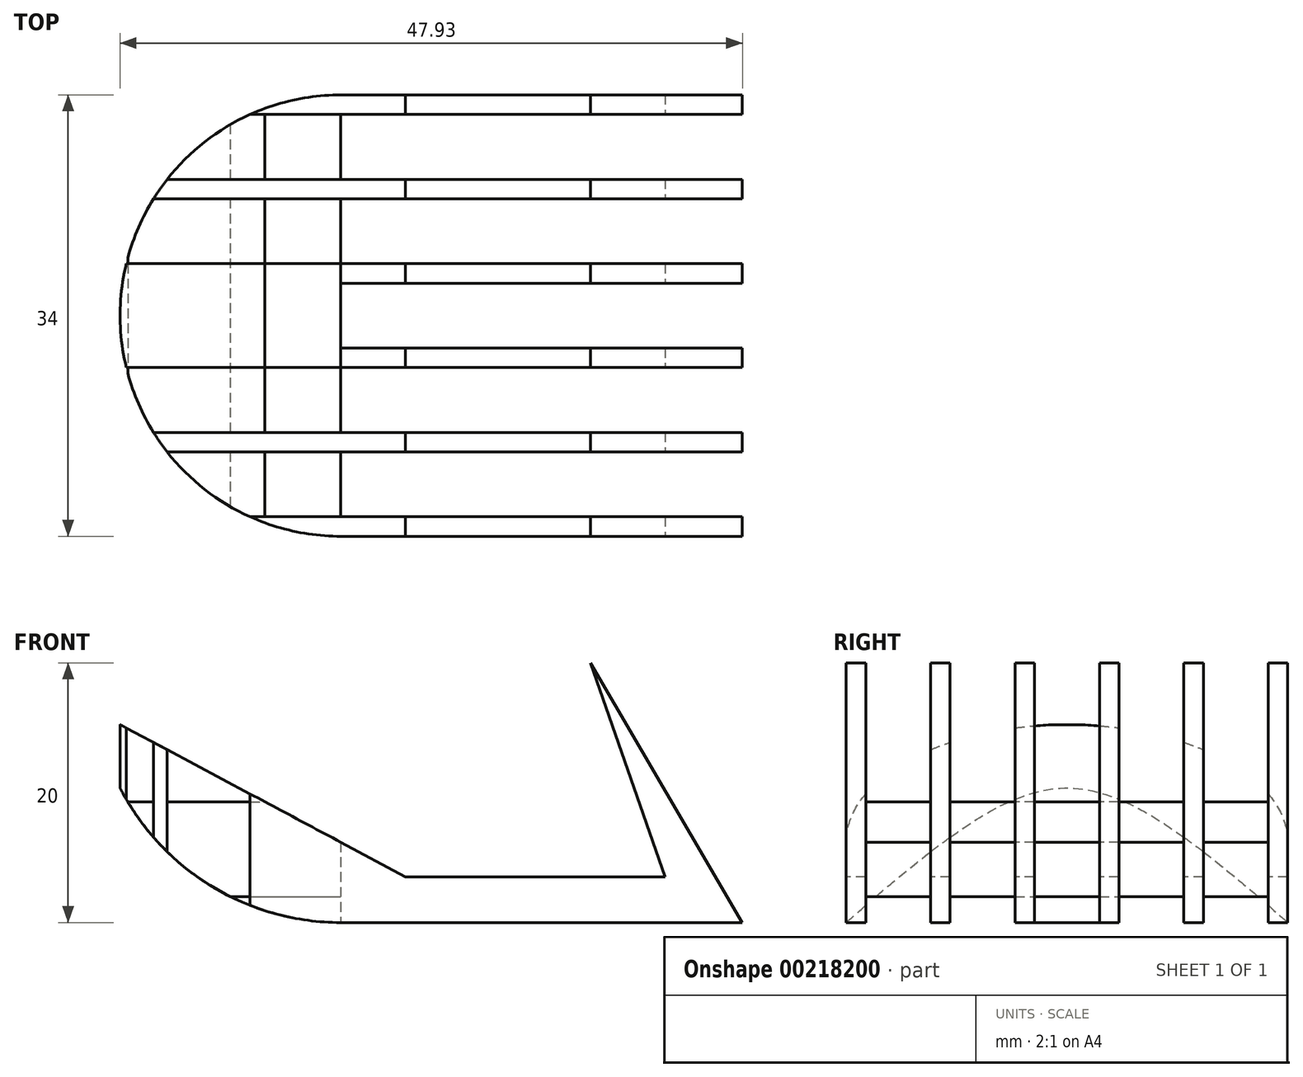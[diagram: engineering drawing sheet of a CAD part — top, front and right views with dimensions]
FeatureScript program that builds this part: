
annotation { "Feature Type Name" : "Feature", "Feature Type Description" : "" }
export const myFeature = defineFeature(function(context is Context, id is Id, definition is map)
    precondition{}
    {
        {
            var Q0;
            Q0=qCreatedBy(makeId("Top.planeOp"),FACE);
            var sketch = newSketch(context, id + "F0", { "sketchPlane" : qUnion([Q0])});
            skLineSegment(sketch, "E0.bottom", {"start": v(0, -14.03) * mm, "end": v(30.93, -14.03) * mm});
            skLineSegment(sketch, "E0.top", {"start": v(0, 19.97) * mm, "end": v(30.93, 19.97) * mm});
            skLineSegment(sketch, "E0.left", {"start": v(0, -14.03) * mm, "end": v(0, 19.97) * mm});
            skLineSegment(sketch, "E0.right", {"start": v(30.93, -14.03) * mm, "end": v(30.93, 19.97) * mm});
            skArc(sketch, "E1", {"start": v(0, 19.97) * mm, "mid": v(-17, 2.97) * mm, "end": v(0, -14.03) * mm});
            skLineSegment(sketch, "E2.bottom", {"start": v(-16.64, -7.53) * mm, "end": v(48.54, -7.53) * mm});
            skLineSegment(sketch, "E2.top", {"start": v(-16.64, -12.53) * mm, "end": v(48.54, -12.53) * mm});
            skLineSegment(sketch, "E2.left", {"start": v(-16.64, -7.53) * mm, "end": v(-16.64, -12.53) * mm});
            skLineSegment(sketch, "E2.right", {"start": v(48.54, -7.53) * mm, "end": v(48.54, -12.53) * mm});
            skPoint(sketch, "E2.middle", {"position": v(15.95, -10.03) * mm});
            skLineSegment(sketch, "E3.0.1.0", {"start": v(-16.64, -6.03) * mm, "end": v(48.54, -6.03) * mm});
            skLineSegment(sketch, "E3.0.1.1", {"start": v(-16.64, -1.03) * mm, "end": v(48.54, -1.03) * mm});
            skLineSegment(sketch, "E3.0.2.0", {"start": v(-16.64, 0.47) * mm, "end": v(48.54, 0.47) * mm});
            skLineSegment(sketch, "E3.0.2.1", {"start": v(-16.64, 5.47) * mm, "end": v(48.54, 5.47) * mm});
            skLineSegment(sketch, "E3.0.3.0", {"start": v(-16.64, 6.97) * mm, "end": v(48.54, 6.97) * mm});
            skLineSegment(sketch, "E3.0.3.1", {"start": v(-16.64, 11.97) * mm, "end": v(48.54, 11.97) * mm});
            skLineSegment(sketch, "E3.0.4.0", {"start": v(-16.64, 13.47) * mm, "end": v(48.54, 13.47) * mm});
            skLineSegment(sketch, "E3.0.4.1", {"start": v(-16.64, 18.47) * mm, "end": v(48.54, 18.47) * mm});
            skLineSegment(sketch, "E3.direction1", {"start": v(-16.64, -12.53) * mm, "end": v(8.36, -12.53) * mm, "construction": true});
            skLineSegment(sketch, "E3.direction2", {"start": v(-16.64, -12.53) * mm, "end": v(-16.64, -6.03) * mm, "construction": true});
            skSolve(sketch);
        }
        {
            var Q0;
            Q0=makeQuery(id+"F0.imprint","IMPRINT",FACE,{"disambiguationData":[TD([[makeQuery(id+"F0.imprint","IMPRINT",EDGE,{"derivedFrom":sQuery(id+"F0.wireOp",EDGE,"E0.bottom")}),1.0]])]});
            var Q1;
            {var subQ0=sQuery(id+"F0.wireOp",EDGE,"E3.0.1.0");var subQ1=sQuery(id+"F0.wireOp",EDGE,"E0.right");var subQ2=makeQuery(id+"F0.imprint","INTERSECT",VERTEX,{"derivedFrom":[subQ1,subQ0]});Q1=makeQuery(id+"F0.imprint","IMPRINT",FACE,{"disambiguationData":[TD([[makeQuery(id+"F0.imprint","IMPRINT",EDGE,{"disambiguationData":[TD([[subQ2,1.0]])],"derivedFrom":subQ1}),1.0]])]});}
            var Q2;
            {var subQ0=sQuery(id+"F0.wireOp",EDGE,"E3.0.1.1");var subQ1=sQuery(id+"F0.wireOp",EDGE,"E0.right");var subQ2=makeQuery(id+"F0.imprint","INTERSECT",VERTEX,{"derivedFrom":[subQ1,subQ0]});Q2=makeQuery(id+"F0.imprint","IMPRINT",FACE,{"disambiguationData":[TD([[makeQuery(id+"F0.imprint","IMPRINT",EDGE,{"disambiguationData":[TD([[subQ2,-1.0]])],"derivedFrom":subQ1}),1.0]])]});}
            var Q3;
            {var subQ0=sQuery(id+"F0.wireOp",EDGE,"E3.0.2.1");var subQ1=sQuery(id+"F0.wireOp",EDGE,"E0.right");var subQ2=makeQuery(id+"F0.imprint","INTERSECT",VERTEX,{"derivedFrom":[subQ1,subQ0]});Q3=makeQuery(id+"F0.imprint","IMPRINT",FACE,{"disambiguationData":[TD([[makeQuery(id+"F0.imprint","IMPRINT",EDGE,{"disambiguationData":[TD([[subQ2,-1.0]])],"derivedFrom":subQ1}),1.0]])]});}
            var Q4;
            {var subQ0=sQuery(id+"F0.wireOp",EDGE,"E3.0.3.1");var subQ1=sQuery(id+"F0.wireOp",EDGE,"E0.right");var subQ2=makeQuery(id+"F0.imprint","INTERSECT",VERTEX,{"derivedFrom":[subQ1,subQ0]});Q4=makeQuery(id+"F0.imprint","IMPRINT",FACE,{"disambiguationData":[TD([[makeQuery(id+"F0.imprint","IMPRINT",EDGE,{"disambiguationData":[TD([[subQ2,-1.0]])],"derivedFrom":subQ1}),1.0]])]});}
            var Q5;
            {var subQ0=sQuery(id+"F0.wireOp",EDGE,"E0.top");Q5=makeQuery(id+"F0.imprint","IMPRINT",FACE,{"disambiguationData":[TD([[makeQuery(id+"F0.imprint","IMPRINT",EDGE,{"derivedFrom":subQ0}),-1.0]])]});}
            var Q6;
            {var subQ0=sQuery(id+"F0.wireOp",EDGE,"E1");var subQ3=sQuery(id+"F0.wireOp",EDGE,"E2.top");var subQ5=makeQuery(id+"F0.imprint","INTERSECT",VERTEX,{"derivedFrom":[subQ0,subQ3]});Q6=makeQuery(id+"F0.imprint","IMPRINT",FACE,{"disambiguationData":[TD([[makeQuery(id+"F0.imprint","IMPRINT",EDGE,{"disambiguationData":[TD([[subQ5,-1.0]])],"derivedFrom":subQ3}),-1.0]])]});}
            var Q7;
            {var subQ0=sQuery(id+"F0.wireOp",EDGE,"E2.bottom");var subQ1=sQuery(id+"F0.wireOp",EDGE,"E0.left");var subQ2=makeQuery(id+"F0.imprint","INTERSECT",VERTEX,{"derivedFrom":[subQ1,subQ0]});Q7=makeQuery(id+"F0.imprint","IMPRINT",FACE,{"disambiguationData":[TD([[makeQuery(id+"F0.imprint","IMPRINT",EDGE,{"disambiguationData":[TD([[subQ2,-1.0]])],"derivedFrom":subQ1}),1.0]])]});}
            var Q8;
            {var subQ0=sQuery(id+"F0.wireOp",EDGE,"E3.0.1.1");var subQ1=sQuery(id+"F0.wireOp",EDGE,"E0.left");var subQ2=makeQuery(id+"F0.imprint","INTERSECT",VERTEX,{"derivedFrom":[subQ1,subQ0]});Q8=makeQuery(id+"F0.imprint","IMPRINT",FACE,{"disambiguationData":[TD([[makeQuery(id+"F0.imprint","IMPRINT",EDGE,{"disambiguationData":[TD([[subQ2,-1.0]])],"derivedFrom":subQ1}),1.0]])]});}
            var Q9;
            {var subQ0=sQuery(id+"F0.wireOp",EDGE,"E3.0.2.1");var subQ1=sQuery(id+"F0.wireOp",EDGE,"E0.left");var subQ2=makeQuery(id+"F0.imprint","INTERSECT",VERTEX,{"derivedFrom":[subQ1,subQ0]});Q9=makeQuery(id+"F0.imprint","IMPRINT",FACE,{"disambiguationData":[TD([[makeQuery(id+"F0.imprint","IMPRINT",EDGE,{"disambiguationData":[TD([[subQ2,-1.0]])],"derivedFrom":subQ1}),1.0]])]});}
            var Q10;
            {var subQ0=sQuery(id+"F0.wireOp",EDGE,"E3.0.3.1");var subQ1=sQuery(id+"F0.wireOp",EDGE,"E0.left");var subQ2=makeQuery(id+"F0.imprint","INTERSECT",VERTEX,{"derivedFrom":[subQ1,subQ0]});Q10=makeQuery(id+"F0.imprint","IMPRINT",FACE,{"disambiguationData":[TD([[makeQuery(id+"F0.imprint","IMPRINT",EDGE,{"disambiguationData":[TD([[subQ2,-1.0]])],"derivedFrom":subQ1}),1.0]])]});}
            var Q11;
            {var subQ0=sQuery(id+"F0.wireOp",EDGE,"E1");var subQ3=sQuery(id+"F0.wireOp",EDGE,"E3.0.4.1");var subQ5=makeQuery(id+"F0.imprint","INTERSECT",VERTEX,{"derivedFrom":[subQ0,subQ3]});Q11=makeQuery(id+"F0.imprint","IMPRINT",FACE,{"disambiguationData":[TD([[makeQuery(id+"F0.imprint","IMPRINT",EDGE,{"disambiguationData":[TD([[subQ5,-1.0]])],"derivedFrom":subQ3}),1.0]])]});}
            extrude(context, id + "F1", {"entities" : qUnion([Q0, Q1, Q2, Q3, Q4, Q5, Q6, Q7, Q8, Q9, Q10, Q11]), "depth" : 20 * mm});
        }
        {
            var Q0;
            {var subQ0=sQuery(id+"F0.wireOp",EDGE,"E2.top");var subQ1=sQuery(id+"F0.wireOp",EDGE,"E0.left");var subQ2=makeQuery(id+"F0.imprint","INTERSECT",VERTEX,{"derivedFrom":[subQ1,subQ0]});Q0=makeQuery(id+"F0.imprint","IMPRINT",FACE,{"disambiguationData":[TD([[makeQuery(id+"F0.imprint","IMPRINT",EDGE,{"disambiguationData":[TD([[subQ2,-1.0]])],"derivedFrom":subQ1}),1.0]])]});}
            var Q1;
            {var subQ0=sQuery(id+"F0.wireOp",EDGE,"E3.0.1.0");var subQ1=sQuery(id+"F0.wireOp",EDGE,"E0.left");var subQ2=makeQuery(id+"F0.imprint","INTERSECT",VERTEX,{"derivedFrom":[subQ1,subQ0]});Q1=makeQuery(id+"F0.imprint","IMPRINT",FACE,{"disambiguationData":[TD([[makeQuery(id+"F0.imprint","IMPRINT",EDGE,{"disambiguationData":[TD([[subQ2,-1.0]])],"derivedFrom":subQ1}),1.0]])]});}
            var Q2;
            {var subQ0=sQuery(id+"F0.wireOp",EDGE,"E3.0.2.0");var subQ1=sQuery(id+"F0.wireOp",EDGE,"E0.left");var subQ2=makeQuery(id+"F0.imprint","INTERSECT",VERTEX,{"derivedFrom":[subQ1,subQ0]});Q2=makeQuery(id+"F0.imprint","IMPRINT",FACE,{"disambiguationData":[TD([[makeQuery(id+"F0.imprint","IMPRINT",EDGE,{"disambiguationData":[TD([[subQ2,-1.0]])],"derivedFrom":subQ1}),1.0]])]});}
            var Q3;
            {var subQ0=sQuery(id+"F0.wireOp",EDGE,"E3.0.3.0");var subQ1=sQuery(id+"F0.wireOp",EDGE,"E0.left");var subQ2=makeQuery(id+"F0.imprint","INTERSECT",VERTEX,{"derivedFrom":[subQ1,subQ0]});Q3=makeQuery(id+"F0.imprint","IMPRINT",FACE,{"disambiguationData":[TD([[makeQuery(id+"F0.imprint","IMPRINT",EDGE,{"disambiguationData":[TD([[subQ2,-1.0]])],"derivedFrom":subQ1}),1.0]])]});}
            var Q4;
            {var subQ0=sQuery(id+"F0.wireOp",EDGE,"E3.0.4.0");var subQ1=sQuery(id+"F0.wireOp",EDGE,"E0.left");var subQ2=makeQuery(id+"F0.imprint","INTERSECT",VERTEX,{"derivedFrom":[subQ1,subQ0]});Q4=makeQuery(id+"F0.imprint","IMPRINT",FACE,{"disambiguationData":[TD([[makeQuery(id+"F0.imprint","IMPRINT",EDGE,{"disambiguationData":[TD([[subQ2,-1.0]])],"derivedFrom":subQ1}),1.0]])]});}
            extrude(context, id + "F2", {"entities" : qUnion([Q0, Q1, Q2, Q3, Q4]), "depth" : 9.3 * mm, "hasSecondDirection" : true, "secondDirectionOppositeDirection" : false, "secondDirectionDepth" : 2 * mm});
        }
        {
            var Q0;
            Q0=makeQuery(id+"F1.opExtrude","SWEPT_FACE",FACE,{"disambiguationData":[OSD([sQuery(id+"F0.wireOp",EDGE,"E0.bottom")])]});
            var sketch = newSketch(context, id + "F3", { "sketchPlane" : qUnion([Q0])});
            skArc(sketch, "E4", {"start": v(-18.91, 16.26) * mm, "mid": v(-12.47, 4.62) * mm, "end": v(0, 0) * mm});
            skLineSegment(sketch, "E5", {"start": v(-18.91, 16.26) * mm, "end": v(4.98, 3.52) * mm});
            skLineSegment(sketch, "E6", {"start": v(4.98, 3.52) * mm, "end": v(24.98, 3.52) * mm});
            skLineSegment(sketch, "E7", {"start": v(24.98, 3.52) * mm, "end": v(19.21, 20) * mm});
            skLineSegment(sketch, "E8", {"start": v(19.21, 20) * mm, "end": v(30.93, 0) * mm});
            skSolve(sketch);
        }
        {
            var Q0;
            {var subQ0=sQuery(id+"F3.wireOp",EDGE,"E4");Q0=makeQuery(id+"F3.imprint","IMPRINT",FACE,{"disambiguationData":[TD([[makeQuery(id+"F3.imprint","IMPRINT",EDGE,{"derivedFrom":subQ0}),1.0]])]});}
            var Q1;
            {var subQ0=sQuery(id+"F3.wireOp",EDGE,"E6");Q1=makeQuery(id+"F3.imprint","IMPRINT",FACE,{"disambiguationData":[TD([[makeQuery(id+"F3.imprint","IMPRINT",EDGE,{"derivedFrom":subQ0}),-1.0]])]});}
            extrude(context, id + "F4", {"entities" : qUnion([Q0, Q1]), "operationType" : NewBodyOperationType.INTERSECT, "oppositeDirection" : true, "depth" : 40 * mm});
        }
    });
